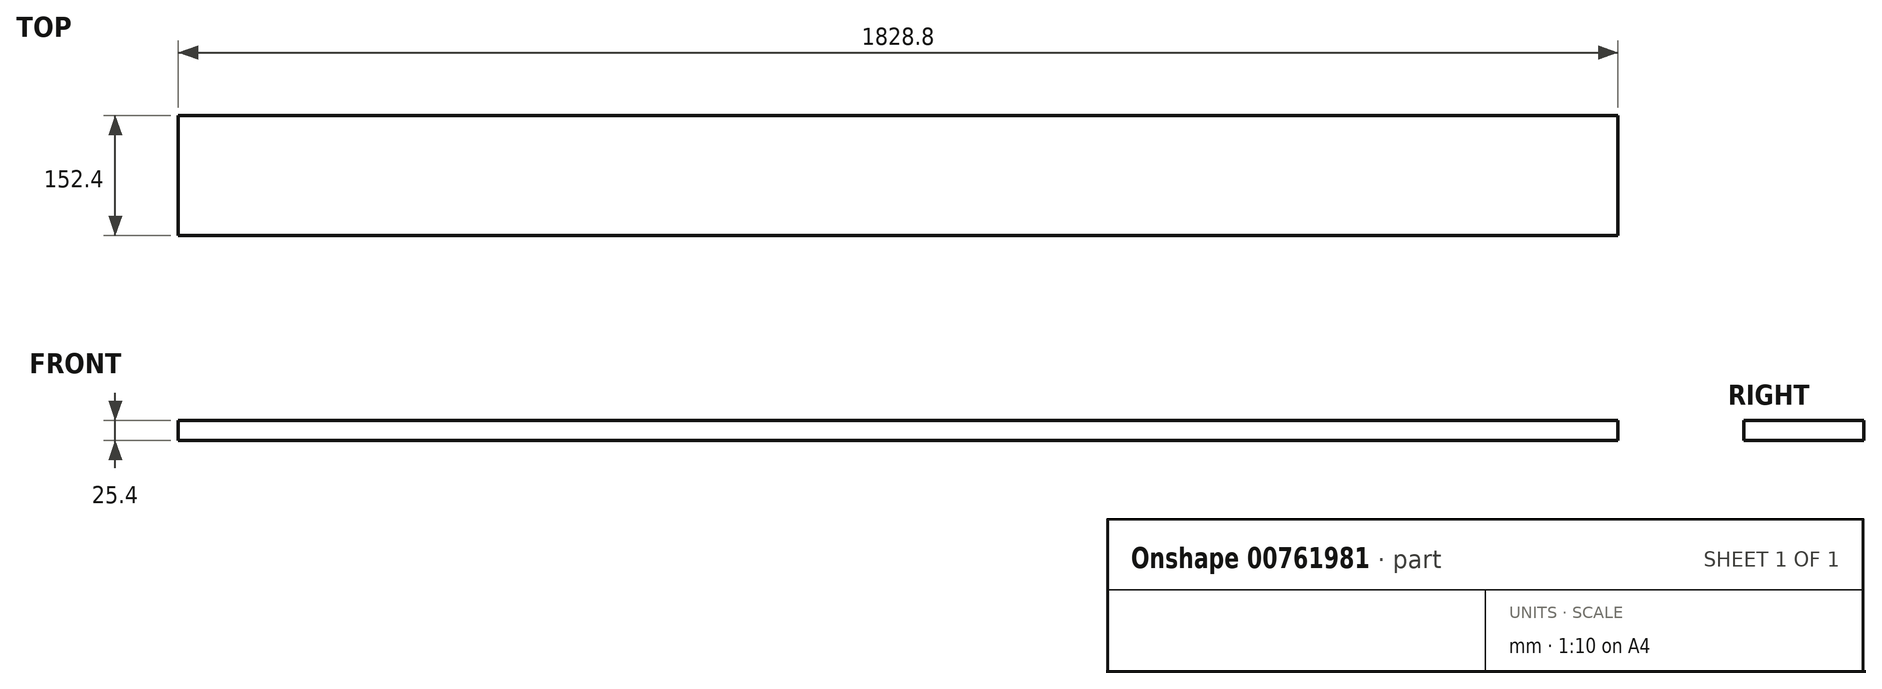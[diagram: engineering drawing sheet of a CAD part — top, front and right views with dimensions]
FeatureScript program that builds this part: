
annotation { "Feature Type Name" : "Feature", "Feature Type Description" : "" }
export const myFeature = defineFeature(function(context is Context, id is Id, definition is map)
    precondition{}
    {
        {
            var Q0;
            Q0=qCreatedBy(makeId("Top.planeOp"),FACE);
            var sketch = newSketch(context, id + "F0", { "sketchPlane" : qUnion([Q0])});
            skLineSegment(sketch, "E0.bottom", {"start": v(-914.4, 76.2) * mm, "end": v(914.4, 76.2) * mm});
            skLineSegment(sketch, "E0.top", {"start": v(-914.4, -76.2) * mm, "end": v(914.4, -76.2) * mm});
            skLineSegment(sketch, "E0.left", {"start": v(-914.4, 76.2) * mm, "end": v(-914.4, -76.2) * mm});
            skLineSegment(sketch, "E0.right", {"start": v(914.4, 76.2) * mm, "end": v(914.4, -76.2) * mm});
            skSolve(sketch);
        }
        {
            var Q0;
            Q0=makeQuery(id+"F0.imprint","IMPRINT",FACE,{"disambiguationData":[TD([[makeQuery(id+"F0.imprint","IMPRINT",EDGE,{"derivedFrom":sQuery(id+"F0.wireOp",EDGE,"E0.bottom")}),-1.0]])]});
            extrude(context, id + "F1", {"entities" : qUnion([Q0]), "depth" : 25.4 * mm, "offsetDistance" : 25.4 * mm});
        }
    });
